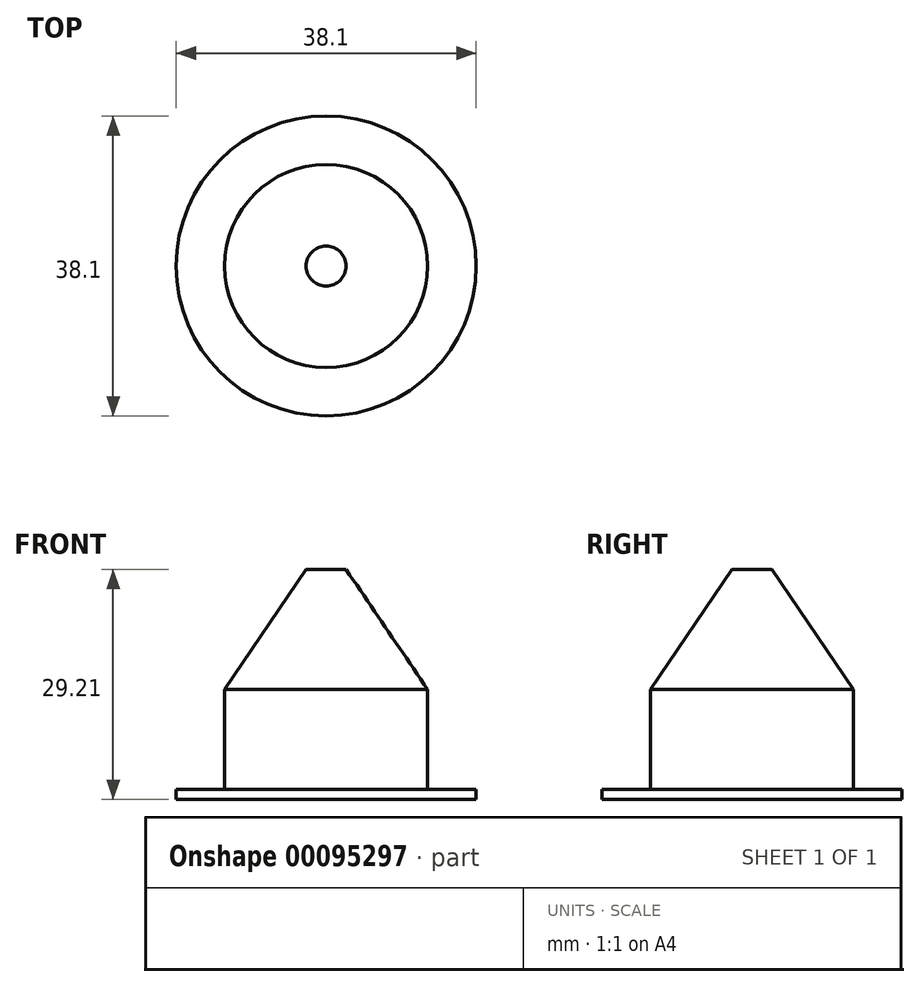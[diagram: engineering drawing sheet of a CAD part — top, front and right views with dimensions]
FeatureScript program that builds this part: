
annotation { "Feature Type Name" : "Feature", "Feature Type Description" : "" }
export const myFeature = defineFeature(function(context is Context, id is Id, definition is map)
    precondition{}
    {
        {
            var Q0;
            Q0=qCreatedBy(makeId("Top.planeOp"),FACE);
            var sketch = newSketch(context, id + "F0", { "sketchPlane" : qUnion([Q0])});
            skCircle(sketch, "E0", {"center": v(0, 0) * mm, "radius": 19.05 * mm});
            skSolve(sketch);
        }
        {
            var Q0;
            Q0 = qSketchRegion(id + "F0", true);
            extrude(context, id + "F1", {"entities" : qUnion([Q0]), "depth" : 1.27 * mm});
        }
        {
            var Q0;
            Q0=makeQuery(id+"F1.opExtrude","CAP_FACE",FACE,{"disambiguationData":[OSD([sQuery(id+"F0.wireOp",EDGE,"E0")])],"isStart":false});
            var sketch = newSketch(context, id + "F2", { "sketchPlane" : qUnion([Q0])});
            skCircle(sketch, "E1", {"center": v(0, 0) * mm, "radius": 12.9 * mm});
            skSolve(sketch);
        }
        {
            var Q0;
            Q0 = qSketchRegion(id + "F2", true);
            extrude(context, id + "F3", {"entities" : qUnion([Q0]), "operationType" : NewBodyOperationType.ADD, "depth" : 12.7 * mm});
        }
        {
            var Q0;
            Q0=qCreatedBy(makeId("Front.planeOp"),FACE);
            var sketch = newSketch(context, id + "F4", { "sketchPlane" : qUnion([Q0])});
            skLineSegment(sketch, "E2", {"start": v(0, 29.21) * mm, "end": v(0, 13.97) * mm});
            skLineSegment(sketch, "E3", {"start": v(0, 29.21) * mm, "end": v(2.54, 29.21) * mm});
            skLineSegment(sketch, "E4", {"start": v(2.54, 29.21) * mm, "end": v(12.9, 13.97) * mm});
            skLineSegment(sketch, "E5", {"start": v(12.9, 13.97) * mm, "end": v(0, 13.97) * mm});
            skSolve(sketch);
        }
        {
            var Q0;
            Q0 = qSketchRegion(id + "F4", true);
            var Q1;
            Q1=makeQuery(id+"F3.opExtrude","SWEPT_FACE",FACE,{"disambiguationData":[OSD([sQuery(id+"F2.wireOp",EDGE,"E1")])]});
            revolve(context, id + "F5", {"operationType" : NewBodyOperationType.ADD, "entities" : qUnion([Q0]), "axis" : qUnion([Q1]), "revolveType" : RevolveType.FULL});
        }
    });
